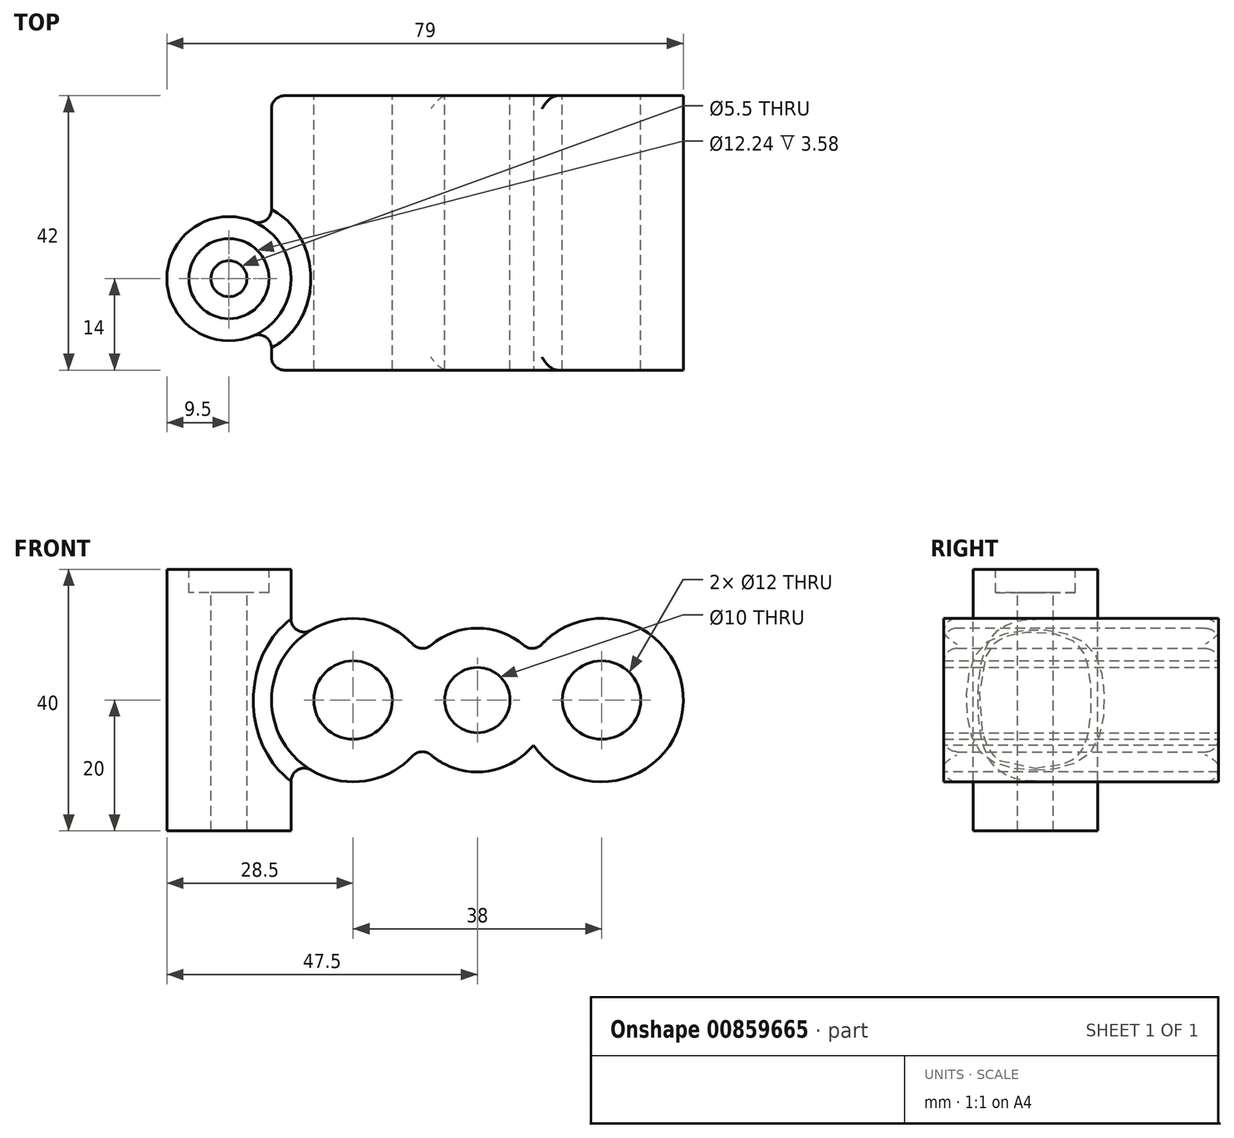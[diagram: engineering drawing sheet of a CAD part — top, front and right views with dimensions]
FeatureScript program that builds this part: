
annotation { "Feature Type Name" : "Feature", "Feature Type Description" : "" }
export const myFeature = defineFeature(function(context is Context, id is Id, definition is map)
    precondition{}
    {
        {
            var Q0;
            Q0=qCreatedBy(makeId("Top.planeOp"),FACE);
            var sketch = newSketch(context, id + "F0", { "sketchPlane" : qUnion([Q0])});
            skCircle(sketch, "E0", {"center": v(0, 0) * mm, "radius": 9.5 * mm});
            skSolve(sketch);
        }
        {
            var Q0;
            Q0=qSketchRegion(id+"F0",true);
            extrude(context, id + "F1", {"entities" : qUnion([Q0]), "endBound" : BoundingType.SYMMETRIC, "oppositeDirection" : true, "depth" : 40 * mm, "offsetDistance" : 25 * mm});
        }
        {
            var Q0;
            Q0=qCreatedBy(makeId("Front.planeOp"),FACE);
            var sketch = newSketch(context, id + "F2", { "sketchPlane" : qUnion([Q0])});
            skArc(sketch, "E1", {"start": v(29.43, 6.9) * mm, "mid": v(6.5, 0) * mm, "end": v(29.43, -6.9) * mm});
            skArc(sketch, "E2", {"start": v(46.57, 6.9) * mm, "mid": v(38, 11) * mm, "end": v(29.43, 6.9) * mm});
            skArc(sketch, "E3", {"start": v(46.57, -6.9) * mm, "mid": v(69.5, 0) * mm, "end": v(46.57, 6.9) * mm});
            skArc(sketch, "E4.trimOffspring", {"start": v(29.43, -6.9) * mm, "mid": v(38, -11) * mm, "end": v(46.57, -6.9) * mm});
            skSolve(sketch);
        }
        {
            var Q0;
            Q0=qSketchRegion(id+"F2",true);
            extrude(context, id + "F3", {"entities" : qUnion([Q0]), "operationType" : NewBodyOperationType.ADD, "oppositeDirection" : true, "depth" : (42 - 14) * mm, "offsetDistance" : 25 * mm, "hasSecondDirection" : true, "secondDirectionOppositeDirection" : false, "secondDirectionDepth" : 14 * mm});
        }
        {
            var Q0;
            Q0=makeQuery(id+"F1.opExtrude","CAP_FACE",FACE,{"disambiguationData":[OSD([sQuery(id+"F0.wireOp",EDGE,"E0")])],"isStart":true});
            var sketch = newSketch(context, id + "F4", { "sketchPlane" : qUnion([Q0])});
            skPoint(sketch, "E5", {"position": v(0, 0) * mm});
            skSolve(sketch);
        }
        {
            var Q0;
            Q0=sQuery(id+"F4.wireOp",VERTEX,"E5");
            var Q1;
            Q1=makeQuery(id+"F1.opExtrude","SWEPT_BODY",BODY,{"disambiguationData":[OSD([sQuery(id+"F0.wireOp",EDGE,"E0")])]});
            hole(context, id + "F5", {"style" : HoleStyle.C_BORE, "endStyle" : HoleEndStyle.THROUGH, "holeDiameter" : 5.5 * mm, "cBoreDiameter" : 12.24 * mm, "cBoreDepth" : 3.58 * mm, "majorDiameter" : 5 * mm, "isTappedThrough" : true, "tappedDepth" : 12 * mm, "tapClearance" : 3, "startFromSketch" : true, "locations" : qUnion([Q0]), "scope" : qUnion([Q1])});
        }
        {
            var Q0;
            Q0=makeQuery(id+"F3.opExtrude","CAP_FACE",FACE,{"disambiguationData":[OSD([sQuery(id+"F2.wireOp",EDGE,"E1"),sQuery(id+"F2.wireOp",EDGE,"E2"),sQuery(id+"F2.wireOp",EDGE,"E3"),sQuery(id+"F2.wireOp",EDGE,"E4.trimOffspring")])],"isStart":false});
            var sketch = newSketch(context, id + "F6", { "sketchPlane" : qUnion([Q0])});
            skPoint(sketch, "E6", {"position": v(-19, 0) * mm});
            skPoint(sketch, "E7", {"position": v(-38, 0) * mm});
            skPoint(sketch, "E8", {"position": v(-57, 0) * mm});
            skSolve(sketch);
        }
        {
            var Q0;
            Q0=sQuery(id+"F6.wireOp",VERTEX,"E6");
            var Q1;
            Q1=sQuery(id+"F6.wireOp",VERTEX,"E8");
            var Q2;
            Q2=makeQuery(id+"F1.opExtrude","SWEPT_BODY",BODY,{"disambiguationData":[OSD([sQuery(id+"F0.wireOp",EDGE,"E0")])]});
            hole(context, id + "F7", {"style" : HoleStyle.SIMPLE, "endStyle" : HoleEndStyle.THROUGH, "holeDiameter" : 12 * mm, "majorDiameter" : 5 * mm, "isTappedThrough" : true, "tappedDepth" : 12 * mm, "tapClearance" : 3, "startFromSketch" : true, "locations" : qUnion([Q0, Q1]), "scope" : qUnion([Q2])});
        }
        {
            var Q0;
            Q0=sQuery(id+"F6.wireOp",VERTEX,"E7");
            var Q1;
            Q1=makeQuery(id+"F1.opExtrude","SWEPT_BODY",BODY,{"disambiguationData":[OSD([sQuery(id+"F0.wireOp",EDGE,"E0")])]});
            hole(context, id + "F8", {"style" : HoleStyle.SIMPLE, "endStyle" : HoleEndStyle.THROUGH, "holeDiameter" : 10 * mm, "majorDiameter" : 5 * mm, "isTappedThrough" : true, "tappedDepth" : 12 * mm, "tapClearance" : 3, "startFromSketch" : true, "locations" : qUnion([Q0]), "scope" : qUnion([Q1])});
        }
        {
            var Q0;
            Q0=makeQuery(id+"F3.opExtrude","SWEPT_FACE",FACE,{"disambiguationData":[OSD([sQuery(id+"F2.wireOp",EDGE,"E2")])]});
            var Q1;
            Q1=makeQuery(id+"F3.opExtrude","SWEPT_FACE",FACE,{"disambiguationData":[OSD([sQuery(id+"F2.wireOp",EDGE,"E1")])]});
            fillet(context, id + "F9", {"entities" : qUnion([Q0, Q1]), "radius" : 2 * mm, "tangentPropagation" : true, "allowEdgeOverflow" : false});
        }
    });
